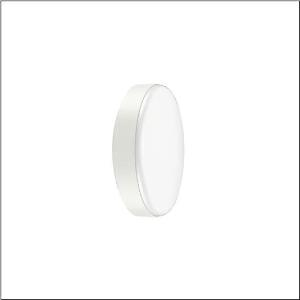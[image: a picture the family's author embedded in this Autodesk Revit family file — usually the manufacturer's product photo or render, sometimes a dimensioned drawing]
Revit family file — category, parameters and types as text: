
# Revit family: rondel_31_51wc10ma42a
name_source: partatom
category: Lighting Fixtures
units: mm (PartAtom-declared; Revit-internal decimal feet)

## family parameters
Cut with Voids When Loaded = No
Host = Face
Light Source = No
Part Type = Normal
Room Calculation Point = No
Round Connector Dimension = Use Diameter
Shared = No

## types (1)
- --- (1 x LED, 2550 lm, 19 W, 4000K)
    Apparent Load = 19 VA
    CIE Flux Codes = 44 75 94 94 100
    Color Rendering = 80
    Color Temperature = 4000K
    Default Elevation = 1800 mm
    Description = Rondel 31, wall and ceiling luminaire, primary optical cover: cover, of PC, opal, light emission: direct distribution, primary light characteristic: symmetric, installation type: surface-mounted, LED, rated luminous flux: 2.550lm, luminous efficacy: 134lm/W, light colour: 840, colour temperature: 4000K, with terminal, 3-pole, max. 2.5mm², mains connection: 220..240V, AC, 50/60Hz, rated input power: 19W, luminaire housing, of PC, traffic white (RAL 9016), diameter: 350mm, protection rating (complete): IP65, insulation class (complete): insulation class II (safety insulation), certification: CE, impact resistance: IK10, permissible operating ambient temperature: -20..+40°C, permissible storage temperature: -20..+60°C, packaging unit: 1 piece
    Height = 97 mm
    Lamp = 1 x LED
    Lamp Light Flux = 2550 lm
    Lamp Power = 19 W
    Lamp count = 1
    Length = 350 mm
    Luminous efficacy = 134 lm/W
    Manufacturer = Siteco
    ModVariant = No
    Model = 51WC10MA42A
    Mounting Place = Ceiling
    Mounting Type = Surface mounted
    Number of Poles = 1
    OnlyDefault = Yes
    Power Factor = 1
    Product Name = Rondel 31
    Product group = wall and ceiling luminaire
    ProductGroupID = 301
    Protection Class = Protection class II
    Protection Degree = IP 65
    RLX_Detail_Level = 1
    RLX_Emergency_Light_Flux = 0 lm
    RLX_Emergency_Type = 0
    RLX_Emergency_Type_DB = No
    RlxData = <blob elided: 30057 chars, md5=130334ce>
    Socket = socket
    Standby Power = 0 W
    System Light Flux = 2550 lm
    System Power = 19 W
    Type Comments = factory setting: luminous flux: 100 % | (ON | ON)
    Type Image = l_1007027.jpg
    URL = http://relux.com
    VarID = @adj_083031
    Voltage = 0 V
    Weight = 0.00 kg
    Width = 0 mm  [stored 0 ft]

note: [stored X ft] marks values corroborated as IEEE doubles in the binary element streams (Revit-internal decimal feet)

## geometry (parser evidence)
native form markers: Blend x4, Sweep x12
no freeform markers — native parametric forms only
